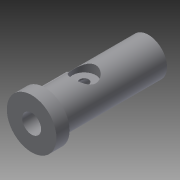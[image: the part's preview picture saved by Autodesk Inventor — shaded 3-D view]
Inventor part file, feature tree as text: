
AUTODESK INVENTOR PART (.ipt)
format: ipt  version: 2015 (Build 190159000, 159)  size: 146,432 bytes
history: native  units: in
note: dims shown in document units (in); Inventor stores cm internally (conversion verified against a paired STEP export)
features: extrude x5, sketch x3, revolve x1, plane x1
ambient origin geometry x8: Origin, YZ Plane, XZ Plane, XY Plane, X Axis, Y Axis, Z Axis, Center Point
bodies: Body1 (feature_tree)
feature tree (10):
  sketch  "Sketch1"  dims[d3=0.7087in d4=0.122in]
  revolve  "Revolution3"  [1 undecoded]
  extrude  "Extrusion8"  Depth=0.3346in
  plane  "Work Plane3"
  extrude  "Extrusion9"  Depth=0.252in
  extrude  "Extrusion10"  Depth=0.1772in
  sketch  "Sketch5"  dims[d7=0.0591in d22=0.252in d27=0.0591in d28=0.0591in d35=0.124in d36=90.0deg d39=0.5906in d40=0.0in d41=0.7087in d42=0.315in d43=0.1181in d44=0.0in d45=0.7874in d46=0.1181in d47=0.0in d48=0.2559in d49=1.0433in d50=0.0in d51=0.6693in d52=0.1772in d53=0.0in]
  extrude  "Extrusion11"  Depth=0.1772in
  extrude  "Extrusion12"  Depth=0.1772in
  sketch  "Sketch4"  dims[d5=0.3346in d6=0.315in]
note: 1 required parameter value undecoded (feature->parameter linkage not recoverable at this tier; creation-order binding heuristic only, values carry confidence <= 0.55)
